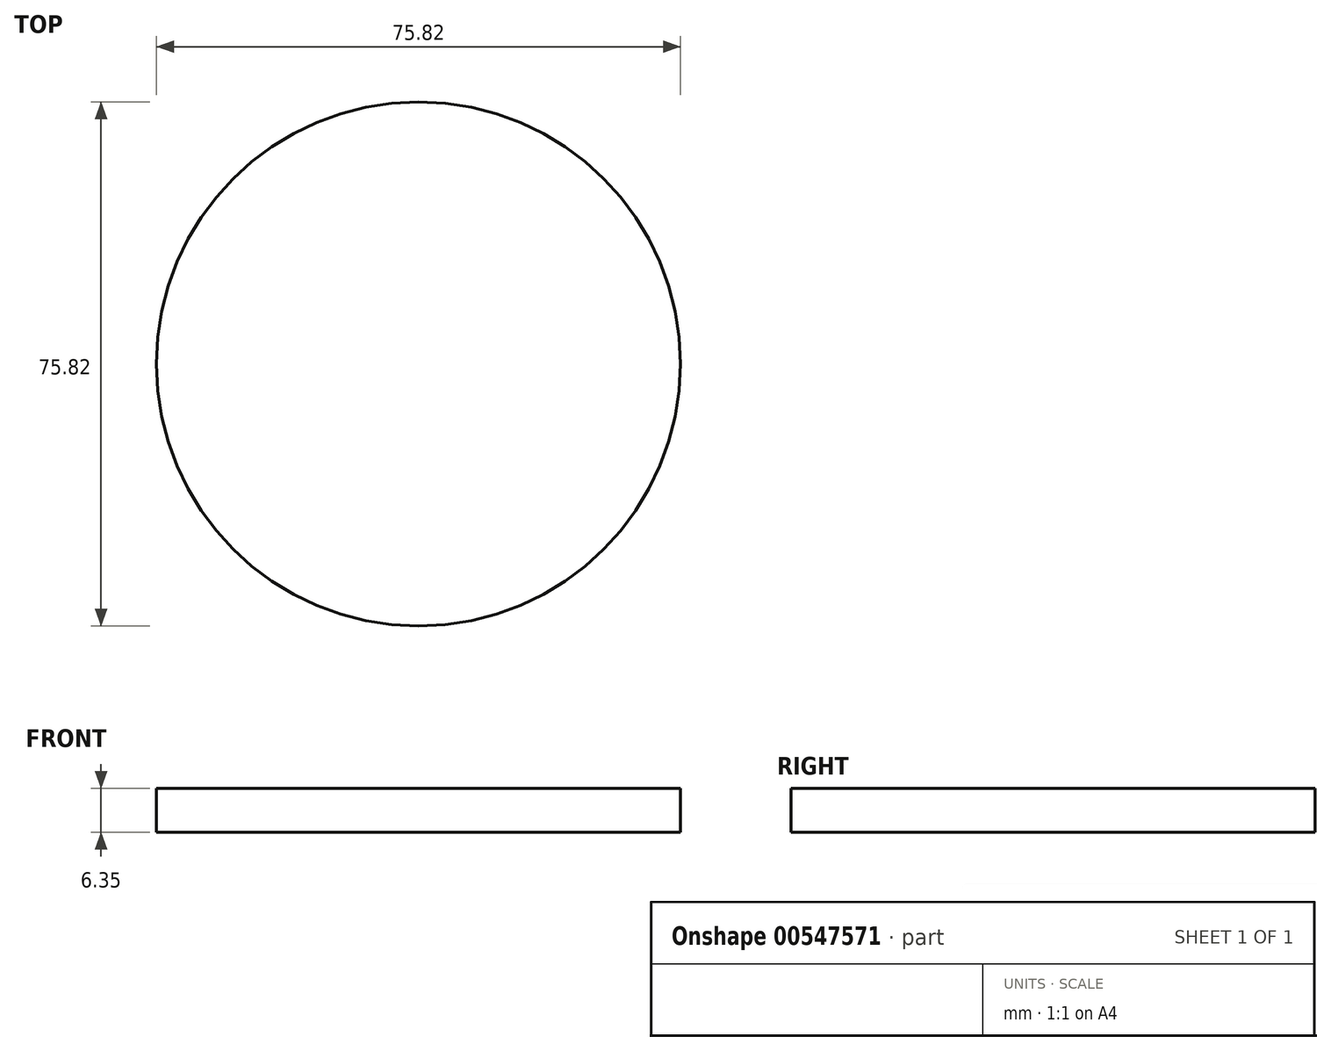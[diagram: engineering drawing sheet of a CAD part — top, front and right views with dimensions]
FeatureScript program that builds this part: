
annotation { "Feature Type Name" : "Feature", "Feature Type Description" : "" }
export const myFeature = defineFeature(function(context is Context, id is Id, definition is map)
    precondition{}
    {
        {
            var Q0;
            Q0=qCreatedBy(makeId("Top.planeOp"),FACE);
            var sketch = newSketch(context, id + "F0", { "sketchPlane" : qUnion([Q0])});
            skCircle(sketch, "E0", {"center": v(0, 0) * mm, "radius": 37.91 * mm});
            skSolve(sketch);
        }
        {
            var Q0;
            Q0=makeQuery(id+"F0.imprint","IMPRINT",FACE,{"disambiguationData":[TD([[makeQuery(id+"F0.imprint","IMPRINT",EDGE,{"derivedFrom":sQuery(id+"F0.wireOp",EDGE,"E0")}),1.0]])]});
            extrude(context, id + "F1", {"entities" : qUnion([Q0]), "depth" : 6.35 * mm, "offsetDistance" : 25.4 * mm});
        }
    });
